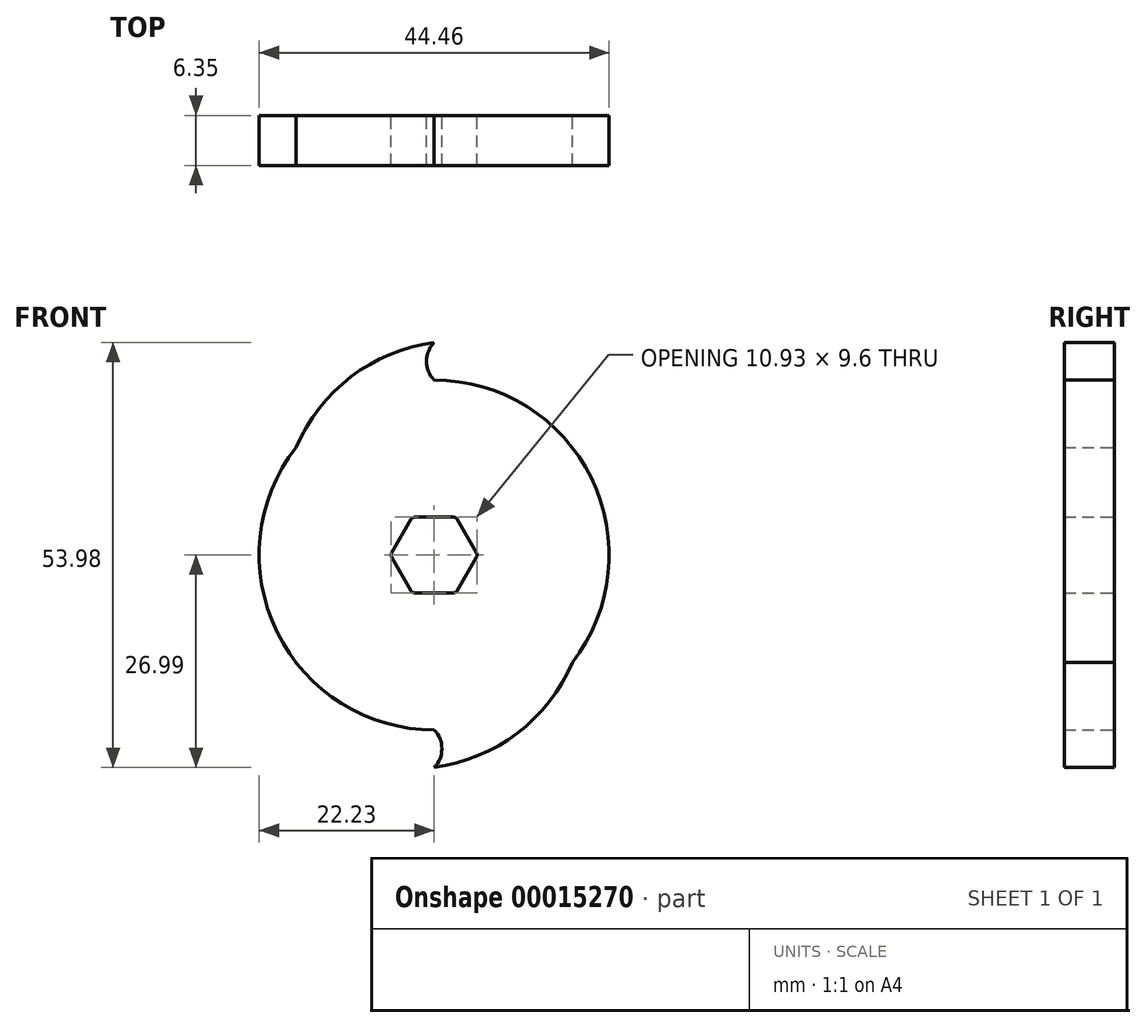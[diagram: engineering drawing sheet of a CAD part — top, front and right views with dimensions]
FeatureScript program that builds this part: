
annotation { "Feature Type Name" : "Feature", "Feature Type Description" : "" }
export const myFeature = defineFeature(function(context is Context, id is Id, definition is map)
    precondition{}
    {
        {
            var Q0;
            Q0=qCreatedBy(makeId("Front.planeOp"),FACE);
            var sketch = newSketch(context, id + "F0", { "sketchPlane" : qUnion([Q0])});
            skCircle(sketch, "E0", {"center": v(0, 0) * mm, "radius": 26.99 * mm, "construction": true});
            skArc(sketch, "E1", {"start": v(17.55, -13.64) * mm, "mid": v(19.96, 9.77) * mm, "end": v(0, 22.22) * mm});
            skArc(sketch, "E2", {"start": v(0, 26.99) * mm, "mid": v(-10.55, 22.65) * mm, "end": v(-17.55, 13.64) * mm});
            skArc(sketch, "E3", {"start": v(0, 26.99) * mm, "mid": v(-0.98, 24.6) * mm, "end": v(0, 22.23) * mm});
            skArc(sketch, "E4.1.0", {"start": v(0, -26.99) * mm, "mid": v(10.55, -22.65) * mm, "end": v(17.55, -13.64) * mm});
            skArc(sketch, "E4.1.1", {"start": v(0, -26.99) * mm, "mid": v(0.98, -24.6) * mm, "end": v(0, -22.22) * mm});
            skArc(sketch, "E5.trimOffspring", {"start": v(-17.55, 13.64) * mm, "mid": v(-19.96, -9.77) * mm, "end": v(0, -22.23) * mm});
            skCircle(sketch, "E6.cCircle", {"center": v(0, 0) * mm, "radius": 4.8 * mm, "construction": true});
            skLineSegment(sketch, "E6.0", {"start": v(-2.48, 4.8) * mm, "end": v(2.48, 4.8) * mm});
            skLineSegment(sketch, "E6.1", {"start": v(2.92, 4.55) * mm, "end": v(5.4, 0.25) * mm});
            skLineSegment(sketch, "E6.2", {"start": v(5.4, -0.25) * mm, "end": v(2.92, -4.55) * mm});
            skLineSegment(sketch, "E6.3", {"start": v(2.48, -4.8) * mm, "end": v(-2.48, -4.8) * mm});
            skLineSegment(sketch, "E6.4", {"start": v(-2.92, -4.55) * mm, "end": v(-5.4, -0.25) * mm});
            skLineSegment(sketch, "E6.5", {"start": v(-5.4, 0.25) * mm, "end": v(-2.92, 4.55) * mm});
            skPoint(sketch, "E6.0.midPoint", {"position": v(0, 4.8) * mm});
            skPoint(sketch, "E7.visualSharp", {"position": v(-2.77, 4.8) * mm});
            skArc(sketch, "E7.filletArc", {"start": v(-2.48, 4.8) * mm, "mid": v(-2.73, 4.73) * mm, "end": v(-2.92, 4.55) * mm});
            skPoint(sketch, "E8.visualSharp", {"position": v(2.77, 4.8) * mm});
            skArc(sketch, "E8.filletArc", {"start": v(2.92, 4.55) * mm, "mid": v(2.73, 4.73) * mm, "end": v(2.48, 4.8) * mm});
            skPoint(sketch, "E9.visualSharp", {"position": v(5.54, 0) * mm});
            skArc(sketch, "E9.filletArc", {"start": v(5.4, -0.25) * mm, "mid": v(5.46, 0) * mm, "end": v(5.4, 0.25) * mm});
            skPoint(sketch, "E10.visualSharp", {"position": v(2.77, -4.8) * mm});
            skArc(sketch, "E10.filletArc", {"start": v(2.48, -4.8) * mm, "mid": v(2.73, -4.73) * mm, "end": v(2.92, -4.55) * mm});
            skPoint(sketch, "E11.visualSharp", {"position": v(-2.77, -4.8) * mm});
            skArc(sketch, "E11.filletArc", {"start": v(-2.92, -4.55) * mm, "mid": v(-2.73, -4.73) * mm, "end": v(-2.48, -4.8) * mm});
            skPoint(sketch, "E12.visualSharp", {"position": v(-5.54, 0) * mm});
            skArc(sketch, "E12.filletArc", {"start": v(-5.4, 0.25) * mm, "mid": v(-5.46, 0) * mm, "end": v(-5.4, -0.25) * mm});
            skSolve(sketch);
        }
        {
            var Q0;
            Q0=makeQuery(id+"F0.imprint","IMPRINT",FACE,{"disambiguationData":[TD([[makeQuery(id+"F0.imprint","IMPRINT",EDGE,{"derivedFrom":sQuery(id+"F0.wireOp",EDGE,"E1")}),1.0]])]});
            extrude(context, id + "F1", {"entities" : qUnion([Q0]), "depth" : 6.35 * mm});
        }
    });
